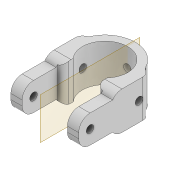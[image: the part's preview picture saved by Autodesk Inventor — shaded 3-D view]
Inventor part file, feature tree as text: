
AUTODESK INVENTOR PART (.ipt)
format: ipt  version: 2022 (Build 260153000, 153)  size: 252,928 bytes
history: native  units: mm
features: extrude x7, sketch x7, fillet x3, projected_geometry x3, mirror x1
ambient origin geometry x8: Origin, YZ Plane, XZ Plane, XY Plane, X Axis, Y Axis, Z Axis, Center Point
bodies: Solid1 (feature_tree)
feature tree (21):
  extrude  "Extrusion1"  Depth=2.0mm
  fillet  "Fillet1"  Radius=8.0mm
  extrude  "Extrusion2"  Depth=1.5mm
  extrude  "Extrusion3"  Depth=1.5mm
  fillet  "Fillet2"  Radius=2.0mm
  mirror  "Mirror1"
  extrude  "Extrusion6"  Depth=100.0mm TaperAngle=0.0deg
  extrude  "Extrusion7"  Depth=2.0mm
  extrude  "Extrusion8"  Depth=5.0mm
  fillet  "Fillet5"  Radius=3.0mm
  extrude  "Extrusion9"  Depth=5.0mm
  sketch  "Sketch1"  dims[d0=12.0mm d1=2.0mm d3=8.0mm]
  sketch  "Sketch2"  dims[d4=1.5mm d5=1.5mm]
  projected_geometry  "Projected Loop1"
  sketch  "Sketch4"  dims[d6=10.0mm d7=0.0mm d8=1.5mm d9=2.0mm]
  projected_geometry  "Projected Loop2"
  projected_geometry  "Projected Loop4"
  sketch  "Sketch7"  dims[d10=2.0mm d12=100.0mm d13=0.0mm]
  sketch  "Sketch8"  dims[d14=2.0mm d15=0.0mm d16=2.0mm]
  sketch  "Sketch9"  dims[d22=3.0mm d28=5.0mm d29=3.0mm]
  sketch  "Sketch10"  dims[d30=2.0mm d31=5.0mm d32=100.0mm d33=0.0mm d34=9.0mm d35=9.0mm d36=1.3mm d37=0.0mm d38=9.0mm d39=9.0mm d40=1.3mm d41=0.0mm d42=2.0mm d43=5.0mm d44=100.0mm d45=0.0mm]
